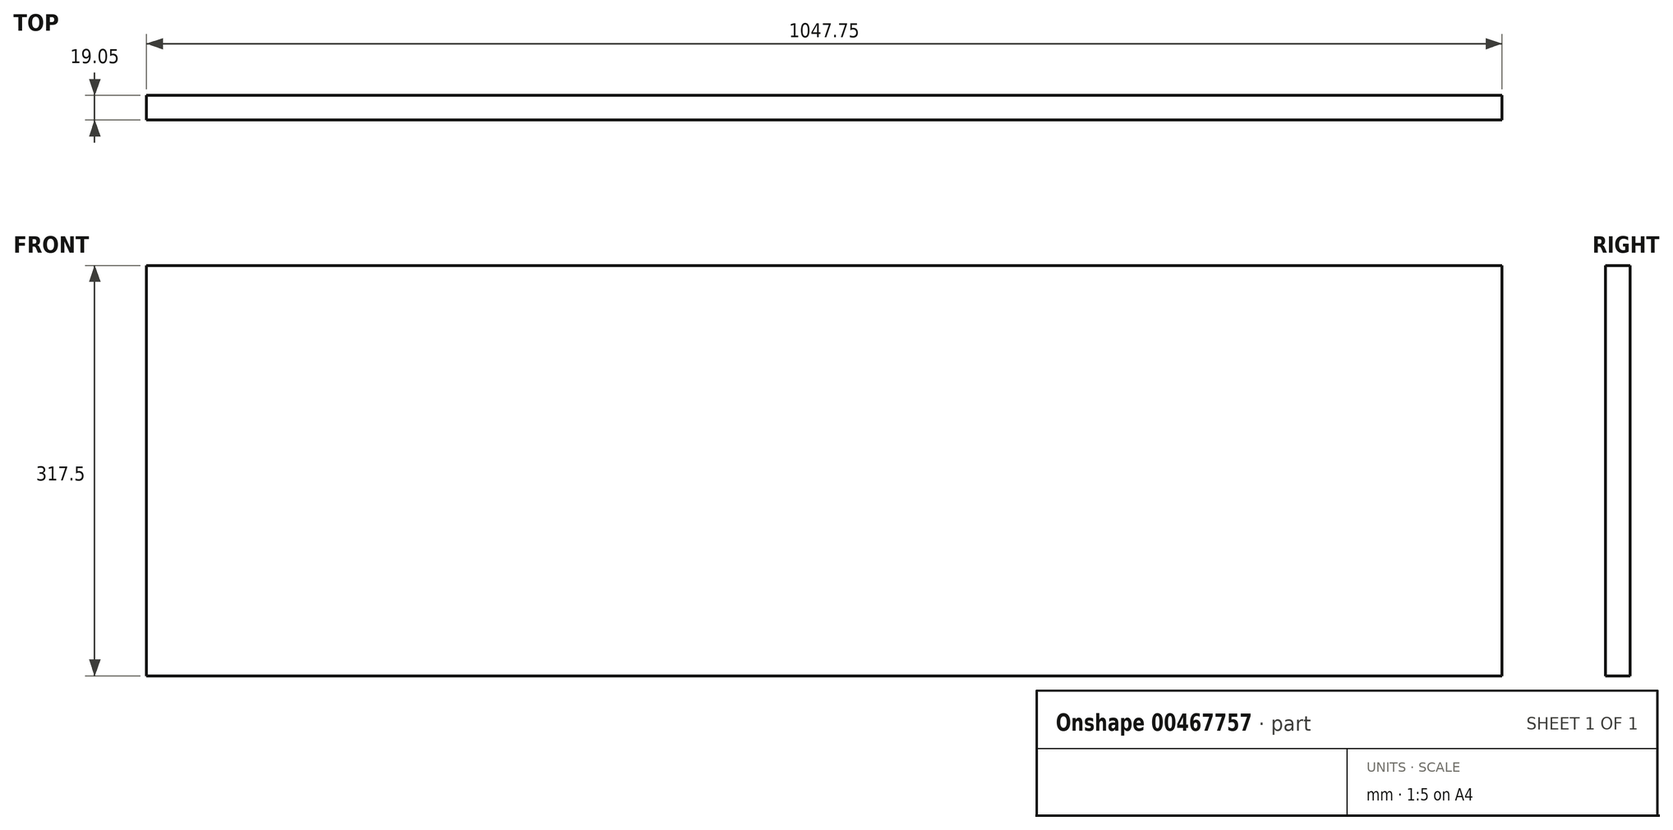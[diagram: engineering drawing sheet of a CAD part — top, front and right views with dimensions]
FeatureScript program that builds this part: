
annotation { "Feature Type Name" : "Feature", "Feature Type Description" : "" }
export const myFeature = defineFeature(function(context is Context, id is Id, definition is map)
    precondition{}
    {
        {
            var Q0;
            Q0=qCreatedBy(makeId("Front.planeOp"),FACE);
            var sketch = newSketch(context, id + "F0", { "sketchPlane" : qUnion([Q0])});
            skLineSegment(sketch, "E0.bottom", {"start": v(0, 0) * mm, "end": v(1047.75, 0) * mm});
            skLineSegment(sketch, "E0.top", {"start": v(0, 317.5) * mm, "end": v(1047.75, 317.5) * mm});
            skLineSegment(sketch, "E0.left", {"start": v(0, 0) * mm, "end": v(0, 317.5) * mm});
            skLineSegment(sketch, "E0.right", {"start": v(1047.75, 0) * mm, "end": v(1047.75, 317.5) * mm});
            skSolve(sketch);
        }
        {
            var Q0;
            Q0=makeQuery(id+"F0.imprint","IMPRINT",FACE,{"disambiguationData":[TD([[makeQuery(id+"F0.imprint","IMPRINT",EDGE,{"derivedFrom":sQuery(id+"F0.wireOp",EDGE,"E0.bottom")}),1.0]])]});
            extrude(context, id + "F1", {"entities" : qUnion([Q0]), "depth" : 19.05 * mm});
        }
    });
